# Revit family: QF_Vollrath_40717
name_source: partatom
category: Specialty Equipment
revit_build: Autodesk Revit 2016 (Build: 20151007_0715(x64)
units: mm (PartAtom-declared; Revit-internal decimal feet)

## family parameters
Always vertical = Yes
Cut with Voids When Loaded = No
OmniClass Number = 23.40.40.14.17.14
OmniClass Title = Hot Plates
Part Type = Normal
Room Calculation Point = No
Round Connector Dimension = Use Diameter
Shared = No
Work Plane-Based = No

## types (1)
- QF_Vollrath_40717
    Apparent Power = 0 VA
    Assembly Code = E1090320
    CSI MasterFormat = 11 44 00
    Conn Plug = NEMA 6-50P
    Cycle = 60 Hz
    Description = Electric Giddle
    Elec Conn Connection Height = 0' - 0"
    Elec Conn RI Height = 0' - 0"
    FL Amps = 38 A
    Manufacturer = Vollrath
    Model = 40717
    Number of Poles = 1
    Phase = 1
    Volts = 220 V
    Watts = 8400 W
    Weight in Pounds = 110

## geometry (parser evidence)
native form markers: Blend x20, Sweep x2
no freeform markers — native parametric forms only
